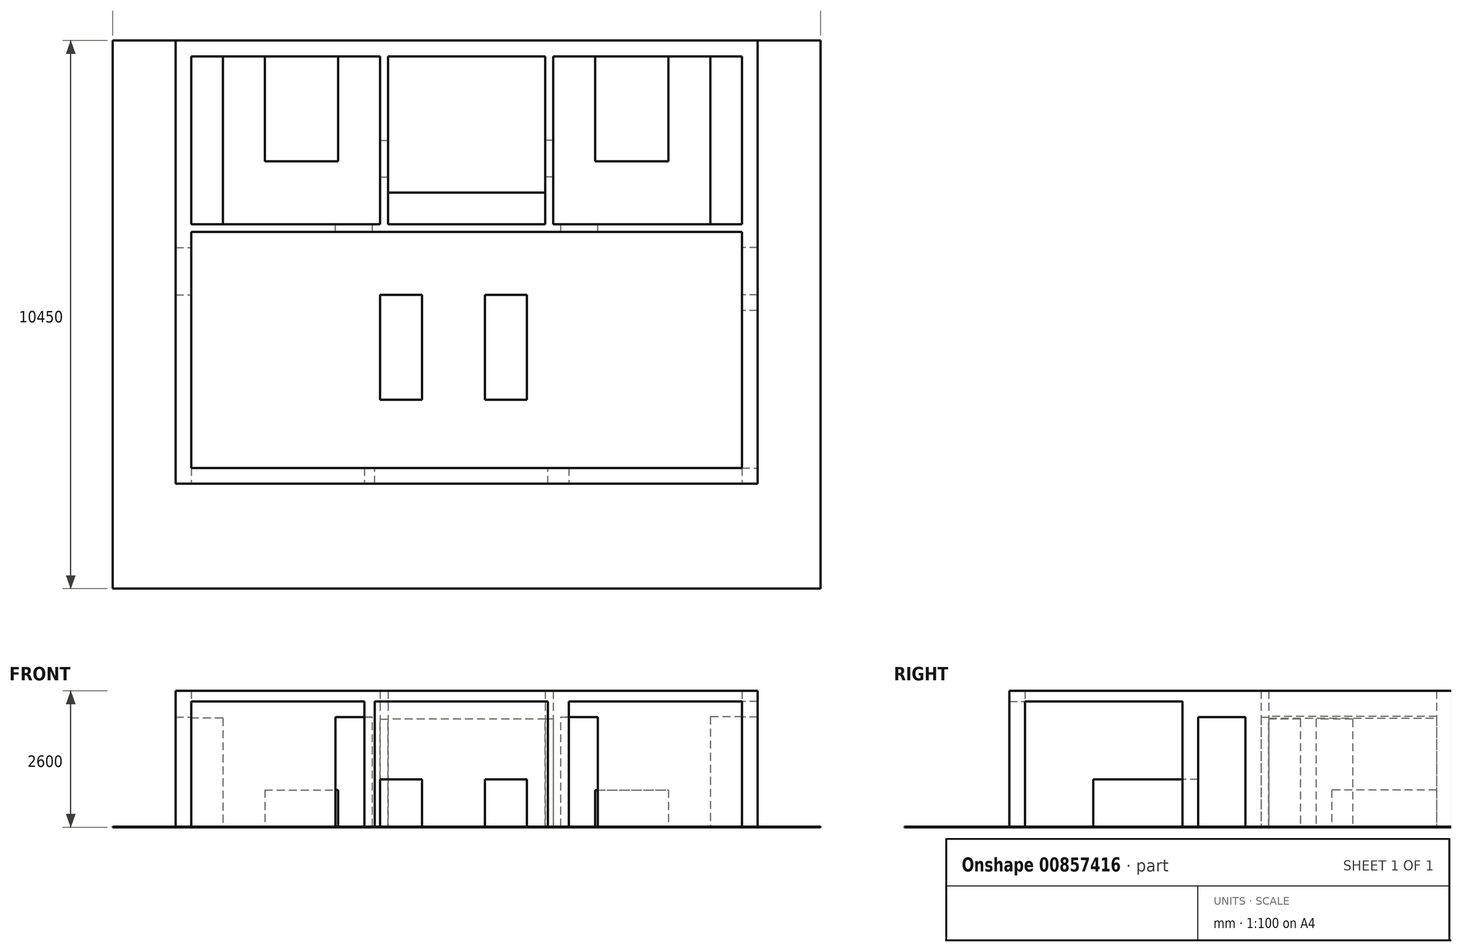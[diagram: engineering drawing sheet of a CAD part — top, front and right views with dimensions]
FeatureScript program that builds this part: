
annotation { "Feature Type Name" : "Feature", "Feature Type Description" : "" }
export const myFeature = defineFeature(function(context is Context, id is Id, definition is map)
    precondition{}
    {
        {
            var Q0;
            Q0=qCreatedBy(makeId("Top.planeOp"),FACE);
            var sketch = newSketch(context, id + "F0", { "sketchPlane" : qUnion([Q0])});
            skLineSegment(sketch, "E0.bottom", {"start": v(0, 0) * mm, "end": v(3600, 0) * mm});
            skLineSegment(sketch, "E0.top", {"start": v(0, 3200) * mm, "end": v(3600, 3200) * mm});
            skLineSegment(sketch, "E0.left", {"start": v(0, 0) * mm, "end": v(0, 3200) * mm});
            skLineSegment(sketch, "E0.right", {"start": v(3600, 0) * mm, "end": v(3600, 3200) * mm});
            skLineSegment(sketch, "E1.bottom", {"start": v(3750, 0) * mm, "end": v(6750, 0) * mm});
            skLineSegment(sketch, "E1.top", {"start": v(3750, 3200) * mm, "end": v(6750, 3200) * mm});
            skLineSegment(sketch, "E1.left", {"start": v(3750, 0) * mm, "end": v(3750, 3200) * mm});
            skLineSegment(sketch, "E1.right", {"start": v(6750, 0) * mm, "end": v(6750, 3200) * mm});
            skLineSegment(sketch, "E2.bottom", {"start": v(6900, 0) * mm, "end": v(10500, 0) * mm});
            skLineSegment(sketch, "E2.top", {"start": v(6900, 3200) * mm, "end": v(10500, 3200) * mm});
            skLineSegment(sketch, "E2.left", {"start": v(6900, 0) * mm, "end": v(6900, 3200) * mm});
            skLineSegment(sketch, "E2.right", {"start": v(10500, 0) * mm, "end": v(10500, 3200) * mm});
            skLineSegment(sketch, "E3.bottom", {"start": v(0, -150) * mm, "end": v(10500, -150) * mm});
            skLineSegment(sketch, "E3.top", {"start": v(0, -4650) * mm, "end": v(10500, -4650) * mm});
            skLineSegment(sketch, "E3.left", {"start": v(0, -150) * mm, "end": v(0, -4650) * mm});
            skLineSegment(sketch, "E3.right", {"start": v(10500, -150) * mm, "end": v(10500, -4650) * mm});
            skLineSegment(sketch, "E4.bottom", {"start": v(-300, -4950) * mm, "end": v(10800, -4950) * mm});
            skLineSegment(sketch, "E4.top", {"start": v(-300, 3500) * mm, "end": v(10800, 3500) * mm});
            skLineSegment(sketch, "E4.left", {"start": v(-300, -4950) * mm, "end": v(-300, 3500) * mm});
            skLineSegment(sketch, "E4.right", {"start": v(10800, -4950) * mm, "end": v(10800, 3500) * mm});
            skSolve(sketch);
        }
        {
            var Q0;
            Q0=makeQuery(id+"F0.imprint","IMPRINT",FACE,{"disambiguationData":[TD([[makeQuery(id+"F0.imprint","IMPRINT",EDGE,{"derivedFrom":sQuery(id+"F0.wireOp",EDGE,"E0.bottom")}),-1.0]])]});
            extrude(context, id + "F1", {"entities" : qUnion([Q0]), "depth" : 2600 * mm, "offsetDistance" : 25 * mm});
        }
        {
            var Q0;
            Q0=makeQuery(id+"F1.opExtrude","SWEPT_FACE",FACE,{"disambiguationData":[OSD([sQuery(id+"F0.wireOp",EDGE,"E0.bottom")])]});
            var sketch = newSketch(context, id + "F2", { "sketchPlane" : qUnion([Q0])});
            skLineSegment(sketch, "E5.bottom", {"start": v(-3450, 0) * mm, "end": v(-2750, 0) * mm});
            skLineSegment(sketch, "E5.top", {"start": v(-3450, 2100) * mm, "end": v(-2750, 2100) * mm});
            skLineSegment(sketch, "E5.left", {"start": v(-3450, 0) * mm, "end": v(-3450, 2100) * mm});
            skLineSegment(sketch, "E5.right", {"start": v(-2750, 0) * mm, "end": v(-2750, 2100) * mm});
            skLineSegment(sketch, "E6.bottom", {"start": v(-7750, 0) * mm, "end": v(-7050, 0) * mm});
            skLineSegment(sketch, "E6.top", {"start": v(-7750, 2100) * mm, "end": v(-7050, 2100) * mm});
            skLineSegment(sketch, "E6.left", {"start": v(-7750, 0) * mm, "end": v(-7750, 2100) * mm});
            skLineSegment(sketch, "E6.right", {"start": v(-7050, 0) * mm, "end": v(-7050, 2100) * mm});
            skSolve(sketch);
        }
        {
            var Q0;
            Q0=makeQuery(id+"F2.imprint","IMPRINT",FACE,{"disambiguationData":[TD([[makeQuery(id+"F2.imprint","IMPRINT",EDGE,{"derivedFrom":sQuery(id+"F2.wireOp",EDGE,"957ca5b5-2eda-4ef8-ae4b-f8e7f074da3f.bottom")}),1.0]])]});
            var Q1;
            Q1=makeQuery(id+"F2.imprint","IMPRINT",FACE,{"disambiguationData":[TD([[makeQuery(id+"F2.imprint","IMPRINT",EDGE,{"derivedFrom":sQuery(id+"F2.wireOp",EDGE,"E6.bottom")}),1.0]])]});
            var Q2;
            Q2=makeQuery(id+"F2.imprint","IMPRINT",FACE,{"disambiguationData":[TD([[makeQuery(id+"F2.imprint","IMPRINT",EDGE,{"derivedFrom":sQuery(id+"F2.wireOp",EDGE,"E5.bottom")}),-1.0]])]});
            extrude(context, id + "F3", {"entities" : qUnion([Q0, Q1, Q2]), "operationType" : NewBodyOperationType.REMOVE, "endBound" : BoundingType.UP_TO_NEXT, "oppositeDirection" : true, "depth" : 25 * mm, "offsetDistance" : 25 * mm});
        }
        {
            var Q0;
            Q0=makeQuery(id+"F1.opExtrude","SWEPT_FACE",FACE,{"disambiguationData":[OSD([sQuery(id+"F0.wireOp",EDGE,"E3.right")])]});
            var sketch = newSketch(context, id + "F4", { "sketchPlane" : qUnion([Q0])});
            skLineSegment(sketch, "E7.bottom", {"start": v(450, 0) * mm, "end": v(1350, 0) * mm});
            skLineSegment(sketch, "E7.top", {"start": v(450, 2100) * mm, "end": v(1350, 2100) * mm});
            skLineSegment(sketch, "E7.left", {"start": v(450, 0) * mm, "end": v(450, 2100) * mm});
            skLineSegment(sketch, "E7.right", {"start": v(1350, 0) * mm, "end": v(1350, 2100) * mm});
            skSolve(sketch);
        }
        {
            var Q0;
            Q0=makeQuery(id+"F4.imprint","IMPRINT",FACE,{"disambiguationData":[TD([[makeQuery(id+"F4.imprint","IMPRINT",EDGE,{"derivedFrom":sQuery(id+"F4.wireOp",EDGE,"E7.bottom")}),1.0]])]});
            extrude(context, id + "F5", {"entities" : qUnion([Q0]), "operationType" : NewBodyOperationType.REMOVE, "endBound" : BoundingType.UP_TO_NEXT, "oppositeDirection" : true, "depth" : 25 * mm, "offsetDistance" : 25 * mm});
        }
        {
            var Q0;
            Q0=makeQuery(id+"F1.opExtrude","SWEPT_FACE",FACE,{"disambiguationData":[OSD([sQuery(id+"F0.wireOp",EDGE,"E3.left")])]});
            var sketch = newSketch(context, id + "F6", { "sketchPlane" : qUnion([Q0])});
            skLineSegment(sketch, "E8.bottom", {"start": v(-450, 0) * mm, "end": v(-1350, 0) * mm});
            skLineSegment(sketch, "E8.top", {"start": v(-450, 2100) * mm, "end": v(-1350, 2100) * mm});
            skLineSegment(sketch, "E8.left", {"start": v(-450, 0) * mm, "end": v(-450, 2100) * mm});
            skLineSegment(sketch, "E8.right", {"start": v(-1350, 0) * mm, "end": v(-1350, 2100) * mm});
            skSolve(sketch);
        }
        {
            var Q0;
            Q0=makeQuery(id+"F6.imprint","IMPRINT",FACE,{"disambiguationData":[TD([[makeQuery(id+"F6.imprint","IMPRINT",EDGE,{"derivedFrom":sQuery(id+"F6.wireOp",EDGE,"E8.bottom")}),-1.0]])]});
            extrude(context, id + "F7", {"entities" : qUnion([Q0]), "operationType" : NewBodyOperationType.REMOVE, "endBound" : BoundingType.UP_TO_NEXT, "oppositeDirection" : true, "depth" : 25 * mm, "offsetDistance" : 25 * mm});
        }
        {
            var Q0;
            Q0=makeQuery(id+"F1.opExtrude","SWEPT_FACE",FACE,{"disambiguationData":[OSD([sQuery(id+"F0.wireOp",EDGE,"E3.right")])]});
            var sketch = newSketch(context, id + "F8", { "sketchPlane" : qUnion([Q0])});
            skLineSegment(sketch, "E9.bottom", {"start": v(1650, 0) * mm, "end": v(4650, 0) * mm});
            skLineSegment(sketch, "E9.top", {"start": v(1650, 2400) * mm, "end": v(4650, 2400) * mm});
            skLineSegment(sketch, "E9.left", {"start": v(1650, 0) * mm, "end": v(1650, 2400) * mm});
            skLineSegment(sketch, "E9.right", {"start": v(4650, 0) * mm, "end": v(4650, 2400) * mm});
            skSolve(sketch);
        }
        {
            var Q0;
            Q0=makeQuery(id+"F1.opExtrude","SWEPT_FACE",FACE,{"disambiguationData":[OSD([sQuery(id+"F0.wireOp",EDGE,"E3.left")])]});
            var sketch = newSketch(context, id + "F9", { "sketchPlane" : qUnion([Q0])});
            skLineSegment(sketch, "E10.bottom", {"start": v(-4650, 0) * mm, "end": v(-1650, 0) * mm});
            skLineSegment(sketch, "E10.top", {"start": v(-4650, 2400) * mm, "end": v(-1650, 2400) * mm});
            skLineSegment(sketch, "E10.left", {"start": v(-4650, 0) * mm, "end": v(-4650, 2400) * mm});
            skLineSegment(sketch, "E10.right", {"start": v(-1650, 0) * mm, "end": v(-1650, 2400) * mm});
            skSolve(sketch);
        }
        {
            var Q0;
            Q0=makeQuery(id+"F8.imprint","IMPRINT",FACE,{"disambiguationData":[TD([[makeQuery(id+"F8.imprint","IMPRINT",EDGE,{"derivedFrom":sQuery(id+"F8.wireOp",EDGE,"E9.bottom")}),1.0]])]});
            extrude(context, id + "F10", {"entities" : qUnion([Q0]), "operationType" : NewBodyOperationType.REMOVE, "endBound" : BoundingType.UP_TO_NEXT, "oppositeDirection" : true, "depth" : 25 * mm, "offsetDistance" : 25 * mm});
        }
        {
            var Q0;
            Q0=makeQuery(id+"F10.boolean.opBoolean","MERGE",FACE,{"derivedFrom":[makeQuery(id+"FudLxrmsEiVxOGA_1.boolean.opBoolean","MERGE",FACE,{"derivedFrom":[makeQuery(id+"F1.opExtrude","SWEPT_FACE",FACE,{"disambiguationData":[OSD([sQuery(id+"F0.wireOp",EDGE,"E3.top")])]}),makeQuery(id+"FudLxrmsEiVxOGA_1.opExtrude","SWEPT_FACE",FACE,{"disambiguationData":[OSD([sQuery(id+"F9.wireOp",EDGE,"E10.left")])]})]}),makeQuery(id+"F10.opExtrude","SWEPT_FACE",FACE,{"disambiguationData":[OSD([sQuery(id+"F8.wireOp",EDGE,"E9.right")])]})]});
            var sketch = newSketch(context, id + "F11", { "sketchPlane" : qUnion([Q0])});
            skLineSegment(sketch, "E11.bottom", {"start": v(-10500, 2400) * mm, "end": v(-7200, 2400) * mm});
            skLineSegment(sketch, "E11.top", {"start": v(-10500, 0) * mm, "end": v(-7200, 0) * mm});
            skLineSegment(sketch, "E11.left", {"start": v(-10500, 2400) * mm, "end": v(-10500, 0) * mm});
            skLineSegment(sketch, "E11.right", {"start": v(-7200, 2400) * mm, "end": v(-7200, 0) * mm});
            skLineSegment(sketch, "E12.bottom", {"start": v(0, 2400) * mm, "end": v(-3300, 2400) * mm});
            skLineSegment(sketch, "E12.top", {"start": v(0, 0) * mm, "end": v(-3300, 0) * mm});
            skLineSegment(sketch, "E12.left", {"start": v(0, 2400) * mm, "end": v(0, 0) * mm});
            skLineSegment(sketch, "E12.right", {"start": v(-3300, 2400) * mm, "end": v(-3300, 0) * mm});
            skLineSegment(sketch, "E13.bottom", {"start": v(-6800, 0) * mm, "end": v(-3500, 0) * mm});
            skLineSegment(sketch, "E13.top", {"start": v(-6800, 2400) * mm, "end": v(-3500, 2400) * mm});
            skLineSegment(sketch, "E13.left", {"start": v(-6800, 0) * mm, "end": v(-6800, 2400) * mm});
            skLineSegment(sketch, "E13.right", {"start": v(-3500, 0) * mm, "end": v(-3500, 2400) * mm});
            skSolve(sketch);
        }
        {
            var Q0;
            Q0=makeQuery(id+"F11.imprint","IMPRINT",FACE,{"disambiguationData":[TD([[makeQuery(id+"F11.imprint","IMPRINT",EDGE,{"derivedFrom":sQuery(id+"F11.wireOp",EDGE,"E11.bottom")}),-1.0]])]});
            var Q1;
            Q1=makeQuery(id+"F11.imprint","IMPRINT",FACE,{"disambiguationData":[TD([[makeQuery(id+"F11.imprint","IMPRINT",EDGE,{"derivedFrom":sQuery(id+"F11.wireOp",EDGE,"E13.bottom")}),-1.0]])]});
            var Q2;
            Q2=makeQuery(id+"F11.imprint","IMPRINT",FACE,{"disambiguationData":[TD([[makeQuery(id+"F11.imprint","IMPRINT",EDGE,{"derivedFrom":sQuery(id+"F11.wireOp",EDGE,"E12.bottom")}),1.0]])]});
            extrude(context, id + "F12", {"entities" : qUnion([Q0, Q1, Q2]), "operationType" : NewBodyOperationType.REMOVE, "endBound" : BoundingType.UP_TO_NEXT, "oppositeDirection" : true, "depth" : 25 * mm, "offsetDistance" : 25 * mm});
        }
        {
            var Q0;
            Q0=qCreatedBy(makeId("Top.planeOp"),FACE);
            var sketch = newSketch(context, id + "F13", { "sketchPlane" : qUnion([Q0])});
            skLineSegment(sketch, "E14.bottom", {"start": v(-1500, -6950) * mm, "end": v(12000, -6950) * mm});
            skLineSegment(sketch, "E14.top", {"start": v(-1500, 3500) * mm, "end": v(12000, 3500) * mm});
            skLineSegment(sketch, "E14.left", {"start": v(-1500, -6950) * mm, "end": v(-1500, 3500) * mm});
            skLineSegment(sketch, "E14.right", {"start": v(12000, -6950) * mm, "end": v(12000, 3500) * mm});
            skSolve(sketch);
        }
        {
            var Q0;
            Q0=makeQuery(id+"F13.imprint","IMPRINT",FACE,{"disambiguationData":[TD([[makeQuery(id+"F13.imprint","IMPRINT",EDGE,{"derivedFrom":sQuery(id+"F13.wireOp",EDGE,"E14.bottom")}),1.0]])]});
            extrude(context, id + "F14", {"entities" : qUnion([Q0]), "operationType" : NewBodyOperationType.ADD, "depth" : 10 * mm, "offsetDistance" : 25 * mm});
        }
        {
            var Q0;
            Q0=makeQuery(id+"F1.opExtrude","SWEPT_FACE",FACE,{"disambiguationData":[OSD([sQuery(id+"F0.wireOp",EDGE,"E0.left")])]});
            var sketch = newSketch(context, id + "F15", { "sketchPlane" : qUnion([Q0])});
            skLineSegment(sketch, "E15.bottom", {"start": v(0, 10) * mm, "end": v(3200, 10) * mm});
            skLineSegment(sketch, "E15.top", {"start": v(0, 2078.05) * mm, "end": v(3200, 2078.05) * mm});
            skLineSegment(sketch, "E15.left", {"start": v(0, 10) * mm, "end": v(0, 2078.05) * mm});
            skLineSegment(sketch, "E15.right", {"start": v(3200, 10) * mm, "end": v(3200, 2078.05) * mm});
            skSolve(sketch);
        }
        {
            var Q0;
            Q0=makeQuery(id+"F15.imprint","IMPRINT",FACE,{"disambiguationData":[TD([[makeQuery(id+"F15.imprint","IMPRINT",EDGE,{"derivedFrom":sQuery(id+"F15.wireOp",EDGE,"E15.bottom")}),1.0]])]});
            extrude(context, id + "F16", {"entities" : qUnion([Q0]), "operationType" : NewBodyOperationType.ADD, "depth" : 600 * mm, "offsetDistance" : 25 * mm});
        }
        {
            var Q0;
            Q0=makeQuery(id+"F1.opExtrude","SWEPT_FACE",FACE,{"disambiguationData":[OSD([sQuery(id+"F0.wireOp",EDGE,"E2.right")])]});
            var sketch = newSketch(context, id + "F17", { "sketchPlane" : qUnion([Q0])});
            skLineSegment(sketch, "E16.bottom", {"start": v(-3200, 10) * mm, "end": v(0, 10) * mm});
            skLineSegment(sketch, "E16.top", {"start": v(-3200, 2110) * mm, "end": v(0, 2110) * mm});
            skLineSegment(sketch, "E16.left", {"start": v(-3200, 10) * mm, "end": v(-3200, 2110) * mm});
            skLineSegment(sketch, "E16.right", {"start": v(0, 10) * mm, "end": v(0, 2110) * mm});
            skSolve(sketch);
        }
        {
            var Q0;
            Q0=makeQuery(id+"F17.imprint","IMPRINT",FACE,{"disambiguationData":[TD([[makeQuery(id+"F17.imprint","IMPRINT",EDGE,{"derivedFrom":sQuery(id+"F17.wireOp",EDGE,"E16.bottom")}),-1.0]])]});
            extrude(context, id + "F18", {"entities" : qUnion([Q0]), "operationType" : NewBodyOperationType.ADD, "depth" : 600 * mm, "offsetDistance" : 25 * mm});
        }
        {
            var Q0;
            Q0=makeQuery(id+"F1.opExtrude","SWEPT_FACE",FACE,{"disambiguationData":[OSD([sQuery(id+"F0.wireOp",EDGE,"E1.bottom")])]});
            var sketch = newSketch(context, id + "F19", { "sketchPlane" : qUnion([Q0])});
            skLineSegment(sketch, "E17.bottom", {"start": v(-6750, 10) * mm, "end": v(-3750, 10) * mm});
            skLineSegment(sketch, "E17.top", {"start": v(-6750, 2059.38) * mm, "end": v(-3750, 2059.38) * mm});
            skLineSegment(sketch, "E17.left", {"start": v(-6750, 10) * mm, "end": v(-6750, 2059.38) * mm});
            skLineSegment(sketch, "E17.right", {"start": v(-3750, 10) * mm, "end": v(-3750, 2059.38) * mm});
            skSolve(sketch);
        }
        {
            var Q0;
            Q0=makeQuery(id+"F19.imprint","IMPRINT",FACE,{"disambiguationData":[TD([[makeQuery(id+"F19.imprint","IMPRINT",EDGE,{"derivedFrom":sQuery(id+"F19.wireOp",EDGE,"E17.bottom")}),-1.0]])]});
            extrude(context, id + "F20", {"entities" : qUnion([Q0]), "operationType" : NewBodyOperationType.ADD, "depth" : 600 * mm, "offsetDistance" : 25 * mm});
        }
        {
            var Q0;
            {var subQ0=sQuery(id+"F13.wireOp",EDGE,"E14.bottom");var subQ1=sQuery(id+"F13.wireOp",EDGE,"E14.top");var subQ2=sQuery(id+"F13.wireOp",EDGE,"E14.left");var subQ3=sQuery(id+"F13.wireOp",EDGE,"E14.right");Q0=makeQuery(id+"F14.boolean.opBoolean","SPLIT",FACE,{"disambiguationData":[TD([makeQuery(id+"F1.opExtrude","SWEPT_FACE",FACE,{"disambiguationData":[OSD([sQuery(id+"F0.wireOp",EDGE,"E0.bottom")])]})])],"derivedFrom":makeQuery(id+"F14.opExtrude","CAP_FACE",FACE,{"disambiguationData":[OSD([subQ0,subQ1,subQ2,subQ3])],"isStart":false})});}
            var sketch = newSketch(context, id + "F21", { "sketchPlane" : qUnion([Q0])});
            skLineSegment(sketch, "E18.bottom", {"start": v(1400, 3200) * mm, "end": v(2800, 3200) * mm});
            skLineSegment(sketch, "E18.top", {"start": v(1400, 1200) * mm, "end": v(2800, 1200) * mm});
            skLineSegment(sketch, "E18.left", {"start": v(1400, 3200) * mm, "end": v(1400, 1200) * mm});
            skLineSegment(sketch, "E18.right", {"start": v(2800, 3200) * mm, "end": v(2800, 1200) * mm});
            skLineSegment(sketch, "E19.bottom", {"start": v(7700, 3200) * mm, "end": v(9100, 3200) * mm});
            skLineSegment(sketch, "E19.top", {"start": v(7700, 1200) * mm, "end": v(9100, 1200) * mm});
            skLineSegment(sketch, "E19.left", {"start": v(7700, 3200) * mm, "end": v(7700, 1200) * mm});
            skLineSegment(sketch, "E19.right", {"start": v(9100, 3200) * mm, "end": v(9100, 1200) * mm});
            skSolve(sketch);
        }
        {
            var Q0;
            Q0=makeQuery(id+"F21.imprint","IMPRINT",FACE,{"disambiguationData":[TD([[makeQuery(id+"F21.imprint","IMPRINT",EDGE,{"derivedFrom":sQuery(id+"F21.wireOp",EDGE,"E18.bottom")}),-1.0]])]});
            extrude(context, id + "F22", {"entities" : qUnion([Q0]), "operationType" : NewBodyOperationType.ADD, "depth" : 700 * mm, "offsetDistance" : 25 * mm});
        }
        {
            var Q0;
            {var subQ0=sQuery(id+"F13.wireOp",EDGE,"E14.bottom");var subQ1=sQuery(id+"F13.wireOp",EDGE,"E14.top");var subQ2=sQuery(id+"F13.wireOp",EDGE,"E14.left");var subQ3=sQuery(id+"F13.wireOp",EDGE,"E14.right");Q0=makeQuery(id+"F14.boolean.opBoolean","SPLIT",FACE,{"disambiguationData":[TD([makeQuery(id+"F1.opExtrude","SWEPT_FACE",FACE,{"disambiguationData":[OSD([sQuery(id+"F0.wireOp",EDGE,"E0.bottom")])]})])],"derivedFrom":makeQuery(id+"F14.opExtrude","CAP_FACE",FACE,{"disambiguationData":[OSD([subQ0,subQ1,subQ2,subQ3])],"isStart":false})});}
            var sketch = newSketch(context, id + "F23", { "sketchPlane" : qUnion([Q0])});
            skLineSegment(sketch, "E20.bottom", {"start": v(7700, 3200) * mm, "end": v(9100, 3200) * mm});
            skLineSegment(sketch, "E20.top", {"start": v(7700, 1200) * mm, "end": v(9100, 1200) * mm});
            skLineSegment(sketch, "E20.left", {"start": v(7700, 3200) * mm, "end": v(7700, 1200) * mm});
            skLineSegment(sketch, "E20.right", {"start": v(9100, 3200) * mm, "end": v(9100, 1200) * mm});
            skSolve(sketch);
        }
        {
            var Q0;
            Q0=makeQuery(id+"F23.imprint","IMPRINT",FACE,{"disambiguationData":[TD([[makeQuery(id+"F23.imprint","IMPRINT",EDGE,{"derivedFrom":sQuery(id+"F23.wireOp",EDGE,"E20.bottom")}),-1.0]])]});
            extrude(context, id + "F24", {"entities" : qUnion([Q0]), "operationType" : NewBodyOperationType.ADD, "depth" : 700 * mm, "offsetDistance" : 25 * mm});
        }
        {
            var Q0;
            Q0=makeQuery(id+"F1.opExtrude","SWEPT_FACE",FACE,{"disambiguationData":[OSD([sQuery(id+"F0.wireOp",EDGE,"E1.right")])]});
            var sketch = newSketch(context, id + "F25", { "sketchPlane" : qUnion([Q0])});
            skLineSegment(sketch, "E21.bottom", {"start": v(-900, 10) * mm, "end": v(-1600, 10) * mm});
            skLineSegment(sketch, "E21.top", {"start": v(-900, 2059.38) * mm, "end": v(-1600, 2059.38) * mm});
            skLineSegment(sketch, "E21.left", {"start": v(-900, 10) * mm, "end": v(-900, 2059.38) * mm});
            skLineSegment(sketch, "E21.right", {"start": v(-1600, 10) * mm, "end": v(-1600, 2059.38) * mm});
            skSolve(sketch);
        }
        {
            var Q0;
            Q0=makeQuery(id+"F25.imprint","IMPRINT",FACE,{"disambiguationData":[TD([[makeQuery(id+"F25.imprint","IMPRINT",EDGE,{"derivedFrom":sQuery(id+"F25.wireOp",EDGE,"E21.bottom")}),-1.0]])]});
            extrude(context, id + "F26", {"entities" : qUnion([Q0]), "operationType" : NewBodyOperationType.REMOVE, "endBound" : BoundingType.UP_TO_NEXT, "oppositeDirection" : true, "depth" : 25 * mm, "offsetDistance" : 25 * mm});
        }
        {
            var Q0;
            Q0=makeQuery(id+"F1.opExtrude","SWEPT_FACE",FACE,{"disambiguationData":[OSD([sQuery(id+"F0.wireOp",EDGE,"E1.left")])]});
            var sketch = newSketch(context, id + "F27", { "sketchPlane" : qUnion([Q0])});
            skLineSegment(sketch, "E22.bottom", {"start": v(900, 10) * mm, "end": v(1600, 10) * mm});
            skLineSegment(sketch, "E22.top", {"start": v(900, 2059.38) * mm, "end": v(1600, 2059.38) * mm});
            skLineSegment(sketch, "E22.left", {"start": v(900, 10) * mm, "end": v(900, 2059.38) * mm});
            skLineSegment(sketch, "E22.right", {"start": v(1600, 10) * mm, "end": v(1600, 2059.38) * mm});
            skSolve(sketch);
        }
        {
            var Q0;
            Q0=makeQuery(id+"F27.imprint","IMPRINT",FACE,{"disambiguationData":[TD([[makeQuery(id+"F27.imprint","IMPRINT",EDGE,{"derivedFrom":sQuery(id+"F27.wireOp",EDGE,"E22.bottom")}),1.0]])]});
            extrude(context, id + "F28", {"entities" : qUnion([Q0]), "operationType" : NewBodyOperationType.REMOVE, "endBound" : BoundingType.UP_TO_NEXT, "oppositeDirection" : true, "depth" : 25 * mm, "offsetDistance" : 25 * mm});
        }
        {
            var Q0;
            {var subQ0=sQuery(id+"F13.wireOp",EDGE,"E14.bottom");var subQ1=sQuery(id+"F13.wireOp",EDGE,"E14.top");var subQ2=sQuery(id+"F13.wireOp",EDGE,"E14.left");var subQ3=sQuery(id+"F13.wireOp",EDGE,"E14.right");var subQ4=makeQuery(id+"F14.opExtrude","CAP_FACE",FACE,{"disambiguationData":[OSD([subQ0,subQ1,subQ2,subQ3])],"isStart":false});Q0=makeQuery(id+"F28.boolean.opBoolean","MERGE",FACE,{"derivedFrom":[makeQuery(id+"F26.boolean.opBoolean","MERGE",FACE,{"derivedFrom":[makeQuery(id+"F14.boolean.opBoolean","SPLIT",FACE,{"disambiguationData":[TD([makeQuery(id+"F1.opExtrude","SWEPT_FACE",FACE,{"disambiguationData":[OSD([sQuery(id+"F0.wireOp",EDGE,"E1.bottom")])]})])],"derivedFrom":subQ4}),makeQuery(id+"F14.boolean.opBoolean","SPLIT",FACE,{"disambiguationData":[TD([makeQuery(id+"F1.opExtrude","SWEPT_FACE",FACE,{"disambiguationData":[OSD([sQuery(id+"F0.wireOp",EDGE,"E0.bottom")])]})])],"derivedFrom":subQ4}),makeQuery(id+"F26.opExtrude","SWEPT_FACE",FACE,{"disambiguationData":[OSD([sQuery(id+"F25.wireOp",EDGE,"E21.bottom")])]})]}),makeQuery(id+"F28.opExtrude","SWEPT_FACE",FACE,{"disambiguationData":[OSD([sQuery(id+"F27.wireOp",EDGE,"E22.bottom")])]})]});}
            var sketch = newSketch(context, id + "F29", { "sketchPlane" : qUnion([Q0])});
            skLineSegment(sketch, "E23.bottom", {"start": v(3601.8, -1350) * mm, "end": v(4401.8, -1350) * mm});
            skLineSegment(sketch, "E23.top", {"start": v(3601.8, -3350) * mm, "end": v(4401.8, -3350) * mm});
            skLineSegment(sketch, "E23.left", {"start": v(3601.8, -1350) * mm, "end": v(3601.8, -3350) * mm});
            skLineSegment(sketch, "E23.right", {"start": v(4401.8, -1350) * mm, "end": v(4401.8, -3350) * mm});
            skLineSegment(sketch, "E24.bottom", {"start": v(5601.8, -1350) * mm, "end": v(6401.8, -1350) * mm});
            skLineSegment(sketch, "E24.top", {"start": v(5601.8, -3350) * mm, "end": v(6401.8, -3350) * mm});
            skLineSegment(sketch, "E24.left", {"start": v(5601.8, -1350) * mm, "end": v(5601.8, -3350) * mm});
            skLineSegment(sketch, "E24.right", {"start": v(6401.8, -1350) * mm, "end": v(6401.8, -3350) * mm});
            skSolve(sketch);
        }
        {
            var Q0;
            Q0=makeQuery(id+"F29.imprint","IMPRINT",FACE,{"disambiguationData":[TD([[makeQuery(id+"F29.imprint","IMPRINT",EDGE,{"derivedFrom":sQuery(id+"F29.wireOp",EDGE,"E23.bottom")}),-1.0]])]});
            var Q1;
            Q1=makeQuery(id+"F29.imprint","IMPRINT",FACE,{"disambiguationData":[TD([[makeQuery(id+"F29.imprint","IMPRINT",EDGE,{"derivedFrom":sQuery(id+"F29.wireOp",EDGE,"E24.bottom")}),-1.0]])]});
            extrude(context, id + "F30", {"entities" : qUnion([Q0, Q1]), "operationType" : NewBodyOperationType.ADD, "depth" : 900 * mm, "offsetDistance" : 25 * mm});
        }
    });
